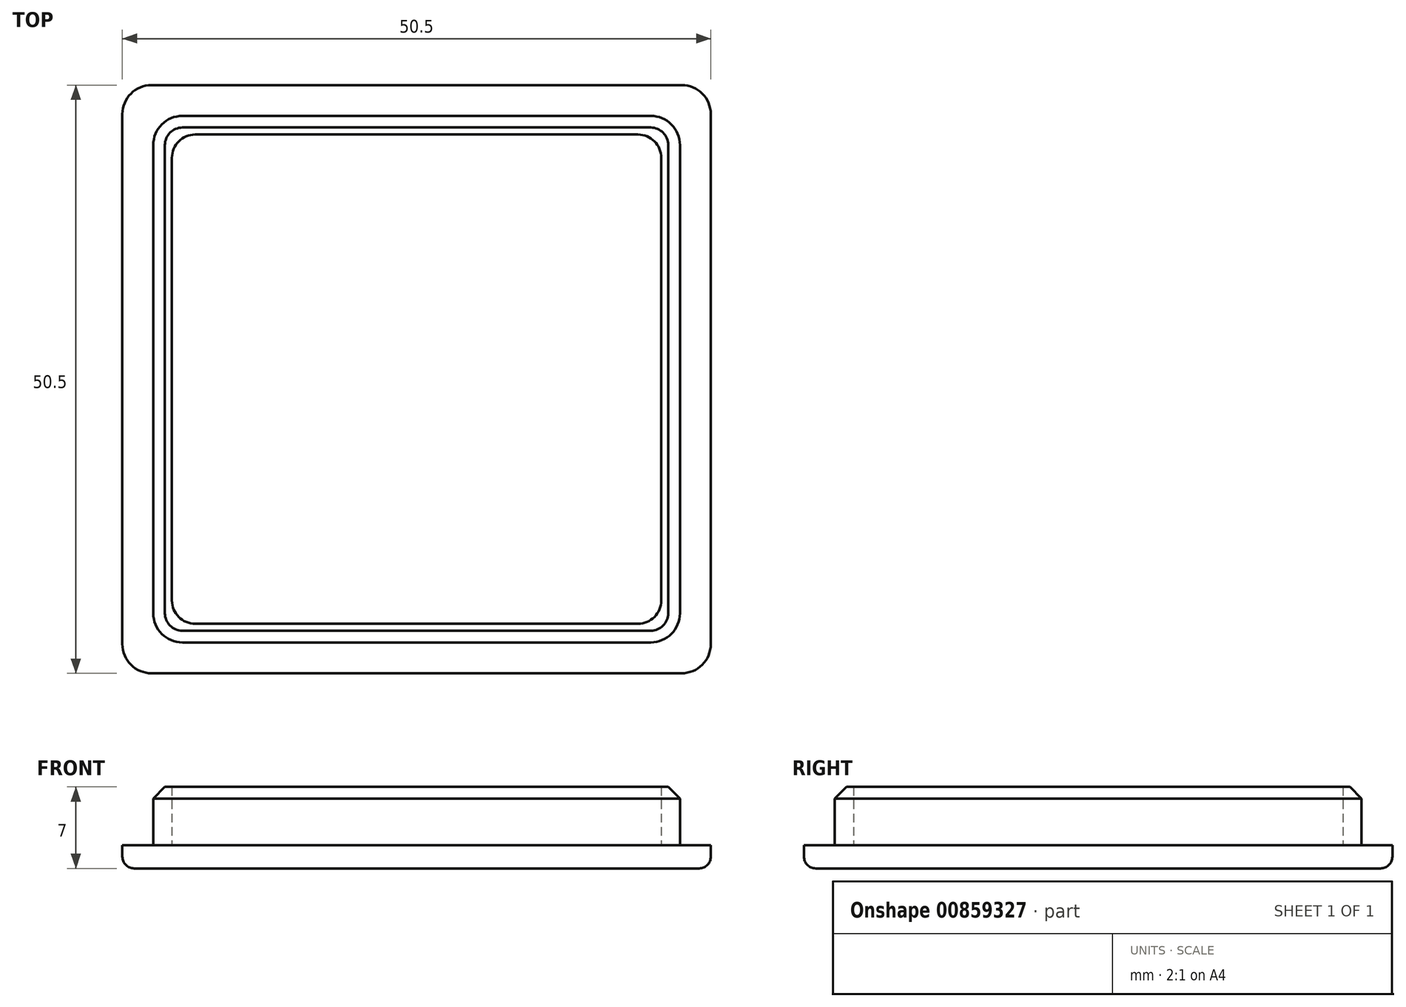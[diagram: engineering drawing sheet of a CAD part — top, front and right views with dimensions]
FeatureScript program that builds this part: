
annotation { "Feature Type Name" : "Feature", "Feature Type Description" : "" }
export const myFeature = defineFeature(function(context is Context, id is Id, definition is map)
    precondition{}
    {
        {
            var Q0;
            Q0=qCreatedBy(makeId("Top.planeOp"),FACE);
            var sketch = newSketch(context, id + "F0", { "sketchPlane" : qUnion([Q0])});
            skLineSegment(sketch, "E0.bottom", {"start": v(25.25, 25.25) * mm, "end": v(-25.25, 25.25) * mm});
            skLineSegment(sketch, "E0.top", {"start": v(25.25, -25.25) * mm, "end": v(-25.25, -25.25) * mm});
            skLineSegment(sketch, "E0.left", {"start": v(25.25, 25.25) * mm, "end": v(25.25, -25.25) * mm});
            skLineSegment(sketch, "E0.right", {"start": v(-25.25, 25.25) * mm, "end": v(-25.25, -25.25) * mm});
            skPoint(sketch, "E0.middle", {"position": v(0, 0) * mm});
            skSolve(sketch);
        }
        {
            var Q0;
            Q0 = qSketchRegion(id + "F0", true);
            extrude(context, id + "F1", {"entities" : qUnion([Q0]), "depth" : 2 * mm, "offsetDistance" : 25 * mm});
        }
        {
            var Q0;
            Q0=makeQuery(id+"F1.opExtrude","CAP_FACE",FACE,{"disambiguationData":[OSD([sQuery(id+"F0.wireOp",EDGE,"E0.bottom"),sQuery(id+"F0.wireOp",EDGE,"E0.top"),sQuery(id+"F0.wireOp",EDGE,"E0.left"),sQuery(id+"F0.wireOp",EDGE,"E0.right")])],"isStart":false});
            var sketch = newSketch(context, id + "F2", { "sketchPlane" : qUnion([Q0])});
            skLineSegment(sketch, "E1.bottom", {"start": v(22.6, 22.6) * mm, "end": v(-22.6, 22.6) * mm});
            skLineSegment(sketch, "E1.top", {"start": v(22.6, -22.6) * mm, "end": v(-22.6, -22.6) * mm});
            skLineSegment(sketch, "E1.left", {"start": v(22.6, 22.6) * mm, "end": v(22.6, -22.6) * mm});
            skLineSegment(sketch, "E1.right", {"start": v(-22.6, 22.6) * mm, "end": v(-22.6, -22.6) * mm});
            skPoint(sketch, "E1.middle", {"position": v(0, 0) * mm});
            skSolve(sketch);
        }
        {
            var Q0;
            Q0 = qSketchRegion(id + "F2", true);
            extrude(context, id + "F3", {"entities" : qUnion([Q0]), "operationType" : NewBodyOperationType.ADD, "depth" : 5 * mm, "offsetDistance" : 25 * mm});
        }
        {
            var Q0;
            Q0=makeQuery(id+"F1.opExtrude","CAP_FACE",FACE,{"disambiguationData":[OSD([sQuery(id+"F0.wireOp",EDGE,"E0.bottom"),sQuery(id+"F0.wireOp",EDGE,"E0.top"),sQuery(id+"F0.wireOp",EDGE,"E0.left"),sQuery(id+"F0.wireOp",EDGE,"E0.right")])],"isStart":false});
            var sketch = newSketch(context, id + "F4", { "sketchPlane" : qUnion([Q0])});
            skLineSegment(sketch, "E2.bottom", {"start": v(21, 21) * mm, "end": v(-21, 21) * mm});
            skLineSegment(sketch, "E2.top", {"start": v(21, -21) * mm, "end": v(-21, -21) * mm});
            skLineSegment(sketch, "E2.left", {"start": v(21, 21) * mm, "end": v(21, -21) * mm});
            skLineSegment(sketch, "E2.right", {"start": v(-21, 21) * mm, "end": v(-21, -21) * mm});
            skPoint(sketch, "E2.middle", {"position": v(0, 0) * mm});
            skSolve(sketch);
        }
        {
            var Q0;
            Q0 = qSketchRegion(id + "F4", true);
            extrude(context, id + "F5", {"entities" : qUnion([Q0]), "operationType" : NewBodyOperationType.REMOVE, "endBound" : BoundingType.UP_TO_NEXT, "depth" : 25 * mm, "offsetDistance" : 25 * mm});
        }
        {
            var Q0;
            Q0=makeQuery(id+"F1.opExtrude","SWEPT_EDGE",EDGE,{"disambiguationData":[OSD([sQuery(id+"F0.wireOp",EDGE,"E0.bottom"),sQuery(id+"F0.wireOp",EDGE,"E0.right")])]});
            var Q1;
            Q1=makeQuery(id+"F1.opExtrude","SWEPT_EDGE",EDGE,{"disambiguationData":[OSD([sQuery(id+"F0.wireOp",EDGE,"E0.top"),sQuery(id+"F0.wireOp",EDGE,"E0.right")])]});
            var Q2;
            Q2=makeQuery(id+"F1.opExtrude","SWEPT_EDGE",EDGE,{"disambiguationData":[OSD([sQuery(id+"F0.wireOp",EDGE,"E0.top"),sQuery(id+"F0.wireOp",EDGE,"E0.left")])]});
            var Q3;
            Q3=makeQuery(id+"F1.opExtrude","SWEPT_EDGE",EDGE,{"disambiguationData":[OSD([sQuery(id+"F0.wireOp",EDGE,"E0.bottom"),sQuery(id+"F0.wireOp",EDGE,"E0.left")])]});
            var Q4;
            Q4=makeQuery(id+"F3.opExtrude","SWEPT_EDGE",EDGE,{"disambiguationData":[OSD([sQuery(id+"F2.wireOp",EDGE,"E1.bottom"),sQuery(id+"F2.wireOp",EDGE,"E1.right")])]});
            var Q5;
            Q5=makeQuery(id+"F3.opExtrude","SWEPT_EDGE",EDGE,{"disambiguationData":[OSD([sQuery(id+"F2.wireOp",EDGE,"E1.top"),sQuery(id+"F2.wireOp",EDGE,"E1.right")])]});
            var Q6;
            Q6=makeQuery(id+"F3.opExtrude","SWEPT_EDGE",EDGE,{"disambiguationData":[OSD([sQuery(id+"F2.wireOp",EDGE,"E1.top"),sQuery(id+"F2.wireOp",EDGE,"E1.left")])]});
            var Q7;
            Q7=makeQuery(id+"F3.opExtrude","SWEPT_EDGE",EDGE,{"disambiguationData":[OSD([sQuery(id+"F2.wireOp",EDGE,"E1.bottom"),sQuery(id+"F2.wireOp",EDGE,"E1.left")])]});
            fillet(context, id + "F6", {"entities" : qUnion([Q0, Q1, Q2, Q3, Q4, Q5, Q6, Q7]), "radius" : 2.5 * mm, "tangentPropagation" : true, "allowEdgeOverflow" : false});
        }
        {
            var Q0;
            Q0=makeQuery(id+"F5.boolean.opBoolean","COPY",EDGE,{"derivedFrom":makeQuery(id+"F5.opExtrude","SWEPT_EDGE",EDGE,{"disambiguationData":[OSD([sQuery(id+"F4.wireOp",EDGE,"E2.bottom"),sQuery(id+"F4.wireOp",EDGE,"E2.right")])]})});
            var Q1;
            Q1=makeQuery(id+"F5.boolean.opBoolean","COPY",EDGE,{"derivedFrom":makeQuery(id+"F5.opExtrude","SWEPT_EDGE",EDGE,{"disambiguationData":[OSD([sQuery(id+"F4.wireOp",EDGE,"E2.bottom"),sQuery(id+"F4.wireOp",EDGE,"E2.left")])]})});
            var Q2;
            Q2=makeQuery(id+"F5.boolean.opBoolean","COPY",EDGE,{"derivedFrom":makeQuery(id+"F5.opExtrude","SWEPT_EDGE",EDGE,{"disambiguationData":[OSD([sQuery(id+"F4.wireOp",EDGE,"E2.top"),sQuery(id+"F4.wireOp",EDGE,"E2.left")])]})});
            var Q3;
            Q3=makeQuery(id+"F5.boolean.opBoolean","COPY",EDGE,{"derivedFrom":makeQuery(id+"F5.opExtrude","SWEPT_EDGE",EDGE,{"disambiguationData":[OSD([sQuery(id+"F4.wireOp",EDGE,"E2.top"),sQuery(id+"F4.wireOp",EDGE,"E2.right")])]})});
            fillet(context, id + "F7", {"entities" : qUnion([Q0, Q1, Q2, Q3]), "radius" : 2 * mm, "tangentPropagation" : true, "allowEdgeOverflow" : false});
        }
        {
            var Q0;
            Q0=makeQuery(id+"F3.opExtrude","CAP_EDGE",EDGE,{"disambiguationData":[OSD([sQuery(id+"F2.wireOp",EDGE,"E1.right")])],"isStart":false});
            chamfer(context, id + "F8", {"entities" : qUnion([Q0]), "width" : 1 * mm, "tangentPropagation" : true});
        }
        {
            var Q0;
            Q0=makeQuery(id+"F1.opExtrude","CAP_EDGE",EDGE,{"disambiguationData":[OSD([sQuery(id+"F0.wireOp",EDGE,"E0.bottom")])],"isStart":true});
            fillet(context, id + "F9", {"entities" : qUnion([Q0]), "radius" : 1 * mm, "tangentPropagation" : true, "allowEdgeOverflow" : false});
        }
    });
